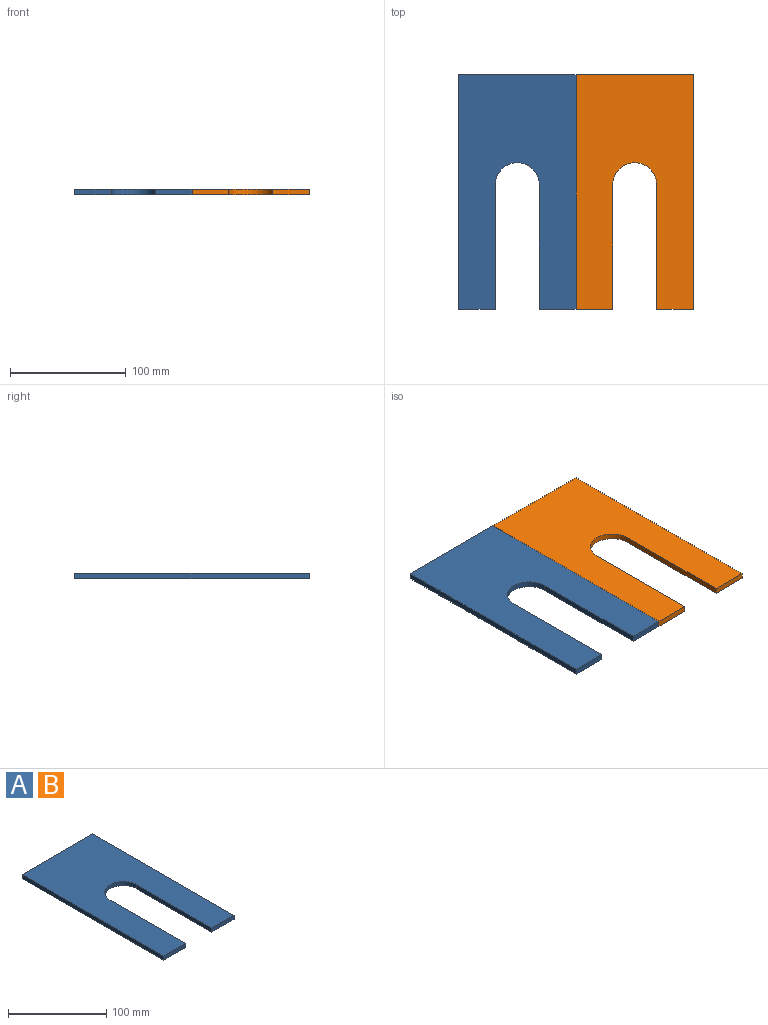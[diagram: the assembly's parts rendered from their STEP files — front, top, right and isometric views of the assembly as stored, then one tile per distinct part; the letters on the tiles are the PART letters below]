
ASSEMBLY  parts=2 mates=1
PART A: 10 faces, bbox 101.6x203.2x5 mm
  f0: plane 107.95x5mm, normal (-1,0,0), area 539.8mm2, adj f1,f7,f8,f9
  f1: plane 31.75x5mm, normal (0,-1,0), area 158.8mm2, adj f0,f2,f8,f9
  f2: plane 203.2x5mm, normal (1,0,0), area 1016mm2, adj f1,f3,f8,f9
  f3: plane 101.6x5mm, normal (0,1,0), area 508mm2, adj f2,f4,f8,f9
  f4: plane 203.2x5mm, normal (-1,0,0), area 1016mm2, adj f3,f5,f8,f9
  f5: plane 31.75x5mm, normal (0,-1,0), area 158.8mm2, adj f4,f6,f8,f9
  f6: plane 107.95x5mm, normal (1,0,0), area 539.8mm2, adj f5,f7,f8,f9
  f7: cylinder r=19.05mm len=38.1mm, axis (0,0,-1), area 299.2mm2, adj f0,f6,f8,f9
  f8: plane 203.2x101.6mm, normal (0,0,1), area 15962.2mm2, adj f0,f1,f2,f3,f4,f5,f6,f7
  f9: plane 203.2x101.6mm, normal (0,0,-1), area 15962.2mm2, adj f0,f1,f2,f3,f4,f5,f6,f7
PART B: same geometry as A
PLACE A t=(-101.6,0,0)mm
PLACE B at identity
MATE fastened A.f2 <-> B.f4  axis (1,0,0) through (-55.27,10.25,2.5)mm
